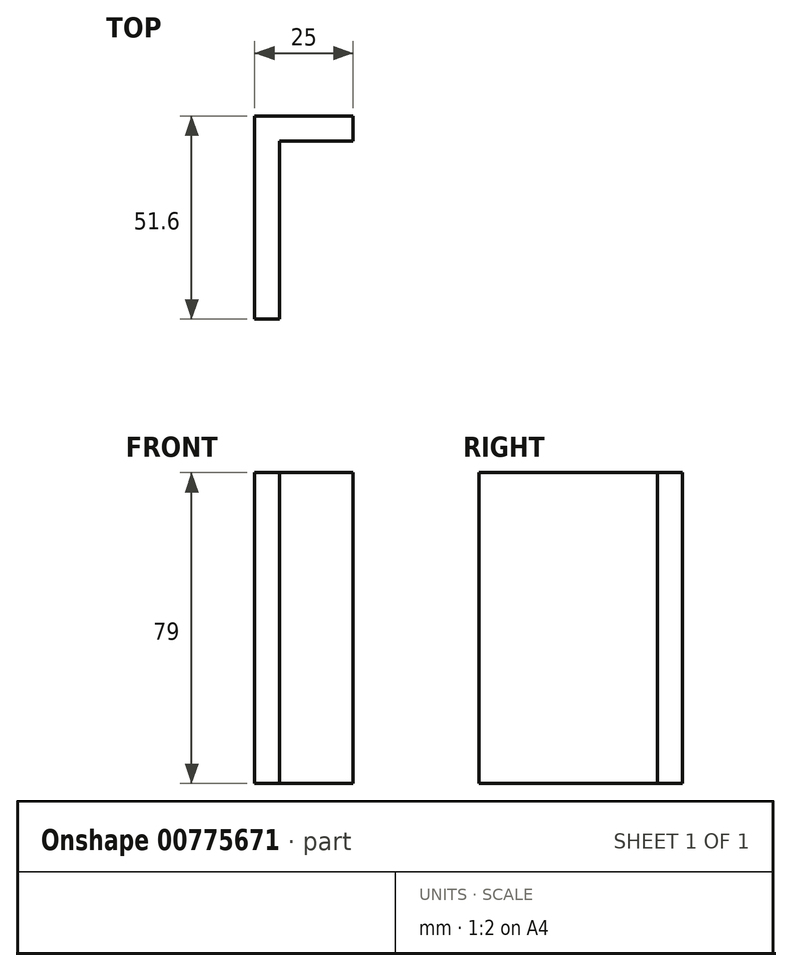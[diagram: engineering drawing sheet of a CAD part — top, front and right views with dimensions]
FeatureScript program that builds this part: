
annotation { "Feature Type Name" : "Feature", "Feature Type Description" : "" }
export const myFeature = defineFeature(function(context is Context, id is Id, definition is map)
    precondition{}
    {
        {
            var Q0;
            Q0=qCreatedBy(makeId("Top.planeOp"),FACE);
            var sketch = newSketch(context, id + "F0", { "sketchPlane" : qUnion([Q0])});
            skLineSegment(sketch, "E0", {"start": v(25, 0) * mm, "end": v(0, 0) * mm});
            skLineSegment(sketch, "E1", {"start": v(0, 0) * mm, "end": v(0, -51.6) * mm});
            skLineSegment(sketch, "E2", {"start": v(0, -51.6) * mm, "end": v(6.35, -51.6) * mm});
            skLineSegment(sketch, "E3", {"start": v(6.35, -51.6) * mm, "end": v(6.35, -6.35) * mm});
            skLineSegment(sketch, "E4", {"start": v(6.35, -6.35) * mm, "end": v(25, -6.35) * mm});
            skLineSegment(sketch, "E5", {"start": v(25, -6.35) * mm, "end": v(25, 0) * mm});
            skSolve(sketch);
        }
        {
            var Q0;
            Q0=makeQuery(id+"F0.imprint","IMPRINT",FACE,{"disambiguationData":[TD([[makeQuery(id+"F0.imprint","IMPRINT",EDGE,{"derivedFrom":sQuery(id+"F0.wireOp",EDGE,"E0")}),1.0]])]});
            extrude(context, id + "F1", {"entities" : qUnion([Q0]), "depth" : 79 * mm, "offsetDistance" : 25 * mm, "symmetric" : true});
        }
    });
